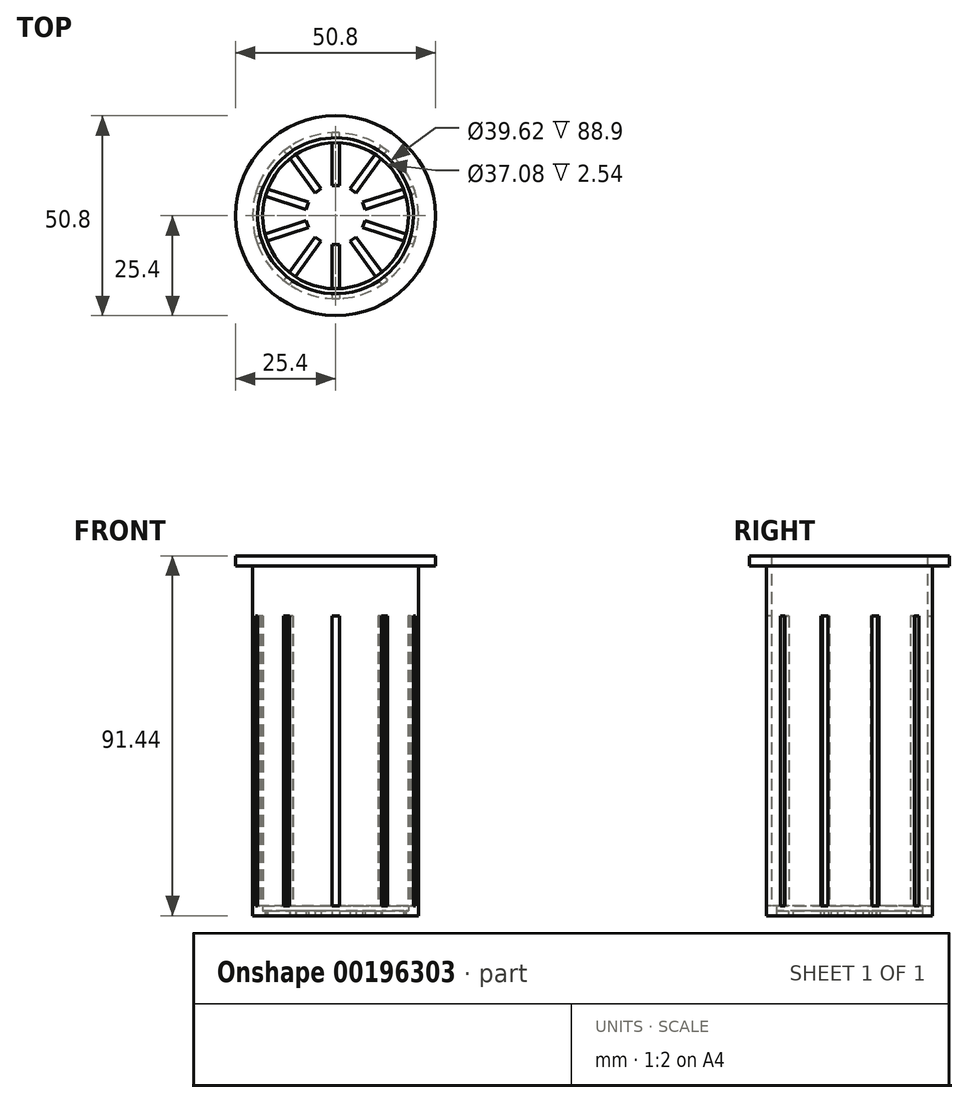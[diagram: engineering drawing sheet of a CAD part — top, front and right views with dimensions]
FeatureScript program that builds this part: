
annotation { "Feature Type Name" : "Feature", "Feature Type Description" : "" }
export const myFeature = defineFeature(function(context is Context, id is Id, definition is map)
    precondition{}
    {
        {
            var Q0;
            Q0=qCreatedBy(makeId("Front.planeOp"),FACE);
            var sketch = newSketch(context, id + "F0", { "sketchPlane" : qUnion([Q0])});
            skLineSegment(sketch, "E0", {"start": v(0, 0) * mm, "end": v(0, 88.9) * mm});
            skLineSegment(sketch, "E1", {"start": v(0, 88.9) * mm, "end": v(0, 91.44) * mm});
            skLineSegment(sketch, "E2", {"start": v(0, 91.44) * mm, "end": v(25.4, 91.44) * mm});
            skLineSegment(sketch, "E3", {"start": v(25.4, 91.44) * mm, "end": v(25.4, 88.9) * mm});
            skLineSegment(sketch, "E4", {"start": v(25.4, 88.9) * mm, "end": v(0, 88.9) * mm});
            skLineSegment(sketch, "E5", {"start": v(0, 88.9) * mm, "end": v(21.08, 88.9) * mm});
            skLineSegment(sketch, "E6", {"start": v(0, 0) * mm, "end": v(21.08, 0) * mm});
            skLineSegment(sketch, "E7", {"start": v(0, 0) * mm, "end": v(0, 2.54) * mm});
            skLineSegment(sketch, "E8", {"start": v(21.08, 88.9) * mm, "end": v(21.08, 0) * mm});
            skSolve(sketch);
        }
        {
            var Q0;
            Q0=qSketchRegion(id+"F0",true);
            var Q1;
            Q1=sQuery(id+"F0.wireOp",EDGE,"E0");
            revolve(context, id + "F1", {"entities" : qUnion([Q0]), "axis" : qUnion([Q1]), "revolveType" : RevolveType.FULL});
        }
        {
            var Q0;
            Q0=makeQuery(id+"F1.opRevolve","SWEPT_FACE",FACE,{"disambiguationData":[OSD([sQuery(id+"F0.wireOp",EDGE,"E2")])]});
            shell(context, id + "F2", {"entities" : qUnion([Q0]), "thickness" : 1.27 * mm});
        }
        {
            var Q0;
            Q0=makeQuery(id+"F2.opShell","OFFSET_FACE",FACE,{"disambiguationData":[OSD([sQuery(id+"F0.wireOp",EDGE,"E4")])]});
            extrude(context, id + "F3", {"entities" : qUnion([Q0]), "operationType" : NewBodyOperationType.ADD, "depth" : 1.27 * mm});
        }
        {
            var Q0;
            Q0=qCreatedBy(makeId("Top.planeOp"),FACE);
            cPlane(context, id + "F4", {"entities" : qUnion([Q0]), "cplaneType" : CPlaneType.OFFSET, "offset" : 88.9 * mm, "width" : 152.4 * mm, "height" : 152.4 * mm});
        }
        {
            var Q0;
            Q0=qCreatedBy(id+"F4.planeOp",FACE);
            var sketch = newSketch(context, id + "F5", { "sketchPlane" : qUnion([Q0])});
            skCircle(sketch, "E9", {"center": v(0, 0) * mm, "radius": 19.69 * mm});
            skSolve(sketch);
        }
        {
            var Q0;
            Q0=qSketchRegion(id+"F5",true);
            extrude(context, id + "F6", {"entities" : qUnion([Q0]), "operationType" : NewBodyOperationType.REMOVE, "depth" : 25.4 * mm});
        }
        {
            var Q0;
            Q0=qCreatedBy(makeId("Top.planeOp"),FACE);
            var sketch = newSketch(context, id + "F7", { "sketchPlane" : qUnion([Q0])});
            skLineSegment(sketch, "E10", {"start": v(0, 0) * mm, "end": v(0, -17.27) * mm});
            skLineSegment(sketch, "E11.bottom", {"start": v(0.95, -7.37) * mm, "end": v(-0.95, -7.37) * mm});
            skLineSegment(sketch, "E11.top", {"start": v(0.95, -27.18) * mm, "end": v(-0.95, -27.18) * mm});
            skLineSegment(sketch, "E11.left", {"start": v(0.95, -7.37) * mm, "end": v(0.95, -27.18) * mm});
            skLineSegment(sketch, "E11.right", {"start": v(-0.95, -7.37) * mm, "end": v(-0.95, -27.18) * mm});
            skPoint(sketch, "E11.middle", {"position": v(0, -17.27) * mm});
            skLineSegment(sketch, "E12.1.0", {"start": v(3.67, -6.48) * mm, "end": v(15.31, -22.51) * mm});
            skLineSegment(sketch, "E12.1.1", {"start": v(5.2, -5.36) * mm, "end": v(16.85, -21.4) * mm});
            skLineSegment(sketch, "E12.1.2", {"start": v(5.2, -5.36) * mm, "end": v(3.67, -6.48) * mm});
            skLineSegment(sketch, "E12.1.3", {"start": v(16.85, -21.4) * mm, "end": v(15.31, -22.51) * mm});
            skLineSegment(sketch, "E12.2.0", {"start": v(6.88, -3.06) * mm, "end": v(25.73, -9.18) * mm});
            skLineSegment(sketch, "E12.2.1", {"start": v(7.47, -1.24) * mm, "end": v(26.31, -7.37) * mm});
            skLineSegment(sketch, "E12.2.2", {"start": v(7.47, -1.24) * mm, "end": v(6.88, -3.06) * mm});
            skLineSegment(sketch, "E12.2.3", {"start": v(26.31, -7.37) * mm, "end": v(25.73, -9.18) * mm});
            skLineSegment(sketch, "E12.3.0", {"start": v(7.47, 1.6) * mm, "end": v(26.31, 7.73) * mm});
            skLineSegment(sketch, "E12.3.1", {"start": v(6.88, 3.42) * mm, "end": v(25.73, 9.54) * mm});
            skLineSegment(sketch, "E12.3.2", {"start": v(6.88, 3.42) * mm, "end": v(7.47, 1.6) * mm});
            skLineSegment(sketch, "E12.3.3", {"start": v(25.73, 9.54) * mm, "end": v(26.31, 7.73) * mm});
            skLineSegment(sketch, "E12.4.0", {"start": v(5.2, 5.73) * mm, "end": v(16.85, 21.76) * mm});
            skLineSegment(sketch, "E12.4.1", {"start": v(3.67, 6.85) * mm, "end": v(15.31, 22.88) * mm});
            skLineSegment(sketch, "E12.4.2", {"start": v(3.67, 6.85) * mm, "end": v(5.2, 5.73) * mm});
            skLineSegment(sketch, "E12.4.3", {"start": v(15.31, 22.88) * mm, "end": v(16.85, 21.76) * mm});
            skLineSegment(sketch, "E12.5.0", {"start": v(0.95, 7.73) * mm, "end": v(0.95, 27.54) * mm});
            skLineSegment(sketch, "E12.5.1", {"start": v(-0.95, 7.73) * mm, "end": v(-0.95, 27.54) * mm});
            skLineSegment(sketch, "E12.5.2", {"start": v(-0.95, 7.73) * mm, "end": v(0.95, 7.73) * mm});
            skLineSegment(sketch, "E12.5.3", {"start": v(-0.95, 27.54) * mm, "end": v(0.95, 27.54) * mm});
            skLineSegment(sketch, "E12.6.0", {"start": v(-3.67, 6.85) * mm, "end": v(-15.31, 22.88) * mm});
            skLineSegment(sketch, "E12.6.1", {"start": v(-5.2, 5.73) * mm, "end": v(-16.85, 21.76) * mm});
            skLineSegment(sketch, "E12.6.2", {"start": v(-5.2, 5.73) * mm, "end": v(-3.67, 6.85) * mm});
            skLineSegment(sketch, "E12.6.3", {"start": v(-16.85, 21.76) * mm, "end": v(-15.31, 22.88) * mm});
            skLineSegment(sketch, "E12.7.0", {"start": v(-6.88, 3.42) * mm, "end": v(-25.73, 9.54) * mm});
            skLineSegment(sketch, "E12.7.1", {"start": v(-7.47, 1.6) * mm, "end": v(-26.31, 7.73) * mm});
            skLineSegment(sketch, "E12.7.2", {"start": v(-7.47, 1.6) * mm, "end": v(-6.88, 3.42) * mm});
            skLineSegment(sketch, "E12.7.3", {"start": v(-26.31, 7.73) * mm, "end": v(-25.73, 9.54) * mm});
            skLineSegment(sketch, "E12.8.0", {"start": v(-7.47, -1.24) * mm, "end": v(-26.31, -7.37) * mm});
            skLineSegment(sketch, "E12.8.1", {"start": v(-6.88, -3.06) * mm, "end": v(-25.73, -9.18) * mm});
            skLineSegment(sketch, "E12.8.2", {"start": v(-6.88, -3.06) * mm, "end": v(-7.47, -1.24) * mm});
            skLineSegment(sketch, "E12.8.3", {"start": v(-25.73, -9.18) * mm, "end": v(-26.31, -7.37) * mm});
            skLineSegment(sketch, "E12.9.0", {"start": v(-5.2, -5.36) * mm, "end": v(-16.85, -21.4) * mm});
            skLineSegment(sketch, "E12.9.1", {"start": v(-3.67, -6.48) * mm, "end": v(-15.31, -22.51) * mm});
            skLineSegment(sketch, "E12.9.2", {"start": v(-3.67, -6.48) * mm, "end": v(-5.2, -5.36) * mm});
            skLineSegment(sketch, "E12.9.3", {"start": v(-15.31, -22.51) * mm, "end": v(-16.85, -21.4) * mm});
            skPoint(sketch, "E12.center", {"position": v(0, 0.18) * mm});
            skSolve(sketch);
        }
        {
            var Q0;
            Q0=qSketchRegion(id+"F7",true);
            extrude(context, id + "F8", {"entities" : qUnion([Q0]), "operationType" : NewBodyOperationType.REMOVE, "depth" : 76.2 * mm});
        }
        {
            var Q0;
            Q0=qCreatedBy(makeId("Front.planeOp"),FACE);
            var sketch = newSketch(context, id + "F9", { "sketchPlane" : qUnion([Q0])});
            skLineSegment(sketch, "E13", {"start": v(0, 0) * mm, "end": v(0, 2.54) * mm});
            skLineSegment(sketch, "E14", {"start": v(0, 0) * mm, "end": v(21.08, 0) * mm});
            skLineSegment(sketch, "E15", {"start": v(21.08, 0) * mm, "end": v(21.08, 2.54) * mm});
            skLineSegment(sketch, "E16", {"start": v(21.08, 2.54) * mm, "end": v(18.54, 2.54) * mm});
            skLineSegment(sketch, "E17", {"start": v(18.54, 2.54) * mm, "end": v(18.54, 0) * mm});
            skSolve(sketch);
        }
        {
            var Q0;
            Q0=qSketchRegion(id+"F9",true);
            var Q1;
            Q1=sQuery(id+"F9.wireOp",EDGE,"E13");
            revolve(context, id + "F10", {"operationType" : NewBodyOperationType.ADD, "entities" : qUnion([Q0]), "axis" : qUnion([Q1]), "revolveType" : RevolveType.FULL});
        }
    });
